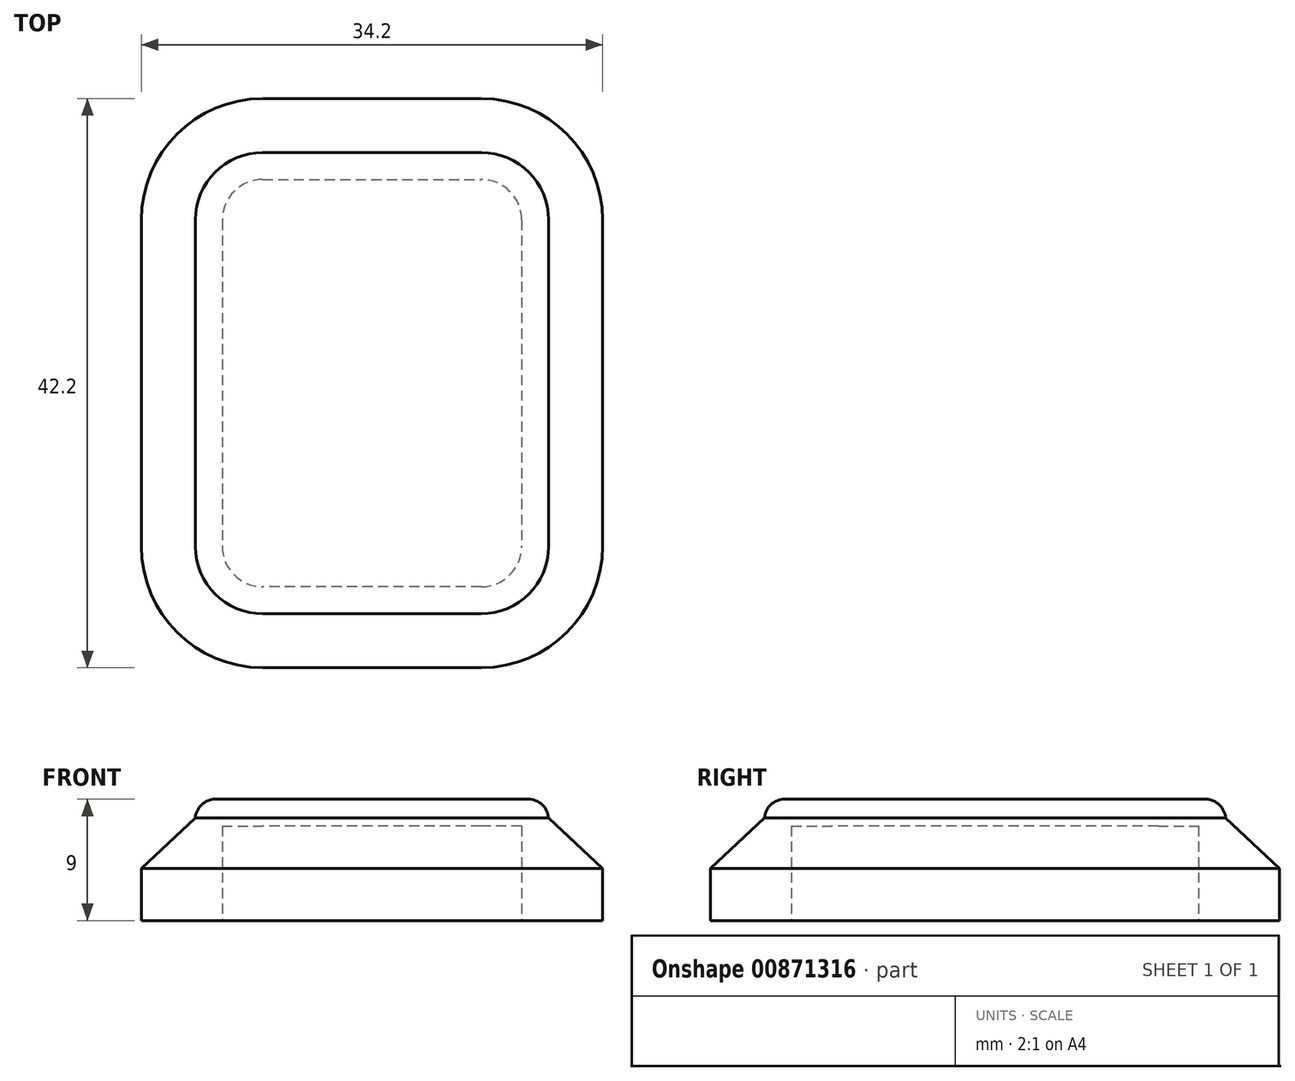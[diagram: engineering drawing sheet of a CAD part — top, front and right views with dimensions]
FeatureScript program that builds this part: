
annotation { "Feature Type Name" : "Feature", "Feature Type Description" : "" }
export const myFeature = defineFeature(function(context is Context, id is Id, definition is map)
    precondition{}
    {
        {
            var Q0;
            Q0=qCreatedBy(makeId("Top.planeOp"),FACE);
            var sketch = newSketch(context, id + "F0", { "sketchPlane" : qUnion([Q0])});
            skLineSegment(sketch, "E0", {"start": v(-8.1, 15.1) * mm, "end": v(8.1, 15.1) * mm});
            skLineSegment(sketch, "E1", {"start": v(11.1, 12.1) * mm, "end": v(11.1, -12.1) * mm});
            skLineSegment(sketch, "E2", {"start": v(8.1, -15.1) * mm, "end": v(-8.1, -15.1) * mm});
            skLineSegment(sketch, "E3", {"start": v(-11.1, 12.1) * mm, "end": v(-11.1, -12.1) * mm});
            skPoint(sketch, "E4.visualSharp", {"position": v(-11.1, 15.1) * mm});
            skArc(sketch, "E4.filletArc", {"start": v(-8.1, 15.1) * mm, "mid": v(-10.22, 14.22) * mm, "end": v(-11.1, 12.1) * mm});
            skPoint(sketch, "E5.visualSharp", {"position": v(11.1, 15.1) * mm});
            skArc(sketch, "E5.filletArc", {"start": v(11.1, 12.1) * mm, "mid": v(10.22, 14.22) * mm, "end": v(8.1, 15.1) * mm});
            skPoint(sketch, "E6.visualSharp", {"position": v(11.1, -15.1) * mm});
            skArc(sketch, "E6.filletArc", {"start": v(8.1, -15.1) * mm, "mid": v(10.22, -14.22) * mm, "end": v(11.1, -12.1) * mm});
            skPoint(sketch, "E7.visualSharp", {"position": v(-11.1, -15.1) * mm});
            skArc(sketch, "E7.filletArc", {"start": v(-11.1, -12.1) * mm, "mid": v(-10.22, -14.22) * mm, "end": v(-8.1, -15.1) * mm});
            skArc(sketch, "E8.0", {"start": v(-8.1, 17.1) * mm, "mid": v(-11.64, 15.64) * mm, "end": v(-13.1, 12.1) * mm});
            skLineSegment(sketch, "E8.1", {"start": v(-13.1, 12.1) * mm, "end": v(-13.1, -12.1) * mm});
            skLineSegment(sketch, "E8.2", {"start": v(-8.1, 17.1) * mm, "end": v(8.1, 17.1) * mm});
            skArc(sketch, "E8.3", {"start": v(-13.1, -12.1) * mm, "mid": v(-11.64, -15.64) * mm, "end": v(-8.1, -17.1) * mm});
            skArc(sketch, "E8.4", {"start": v(13.1, 12.1) * mm, "mid": v(11.64, 15.64) * mm, "end": v(8.1, 17.1) * mm});
            skLineSegment(sketch, "E8.5", {"start": v(13.1, 12.1) * mm, "end": v(13.1, -12.1) * mm});
            skArc(sketch, "E8.6", {"start": v(8.1, -17.1) * mm, "mid": v(11.64, -15.64) * mm, "end": v(13.1, -12.1) * mm});
            skLineSegment(sketch, "E8.7", {"start": v(8.1, -17.1) * mm, "end": v(-8.1, -17.1) * mm});
            skSolve(sketch);
        }
        {
            var Q0;
            Q0 = qSketchRegion(id + "F0", true);
            extrude(context, id + "F1", {"entities" : qUnion([Q0]), "depth" : 7 * mm, "offsetDistance" : 25 * mm});
        }
        {
            var Q0;
            Q0=makeQuery(id+"F1.opExtrude","CAP_FACE",FACE,{"disambiguationData":[OSD([sQuery(id+"F0.wireOp",EDGE,"E0"),sQuery(id+"F0.wireOp",EDGE,"E1"),sQuery(id+"F0.wireOp",EDGE,"E2"),sQuery(id+"F0.wireOp",EDGE,"E3"),sQuery(id+"F0.wireOp",EDGE,"E4.filletArc"),sQuery(id+"F0.wireOp",EDGE,"E5.filletArc"),sQuery(id+"F0.wireOp",EDGE,"E6.filletArc"),sQuery(id+"F0.wireOp",EDGE,"E7.filletArc"),sQuery(id+"F0.wireOp",EDGE,"E8.0"),sQuery(id+"F0.wireOp",EDGE,"E8.1"),sQuery(id+"F0.wireOp",EDGE,"E8.2"),sQuery(id+"F0.wireOp",EDGE,"E8.3"),sQuery(id+"F0.wireOp",EDGE,"E8.4"),sQuery(id+"F0.wireOp",EDGE,"E8.5"),sQuery(id+"F0.wireOp",EDGE,"E8.6"),sQuery(id+"F0.wireOp",EDGE,"E8.7")])],"isStart":false});
            var sketch = newSketch(context, id + "F2", { "sketchPlane" : qUnion([Q0])});
            skArc(sketch, "E9.0", {"start": v(-8.1, 17.1) * mm, "mid": v(-11.64, 15.64) * mm, "end": v(-13.1, 12.1) * mm});
            skLineSegment(sketch, "E9.1", {"start": v(-13.1, 12.1) * mm, "end": v(-13.1, -12.1) * mm});
            skLineSegment(sketch, "E9.2", {"start": v(-8.1, 17.1) * mm, "end": v(8.1, 17.1) * mm});
            skArc(sketch, "E9.3", {"start": v(-13.1, -12.1) * mm, "mid": v(-11.64, -15.64) * mm, "end": v(-8.1, -17.1) * mm});
            skArc(sketch, "E9.4", {"start": v(13.1, 12.1) * mm, "mid": v(11.64, 15.64) * mm, "end": v(8.1, 17.1) * mm});
            skLineSegment(sketch, "E9.5", {"start": v(13.1, 12.1) * mm, "end": v(13.1, -12.1) * mm});
            skArc(sketch, "E9.6", {"start": v(8.1, -17.1) * mm, "mid": v(11.64, -15.64) * mm, "end": v(13.1, -12.1) * mm});
            skLineSegment(sketch, "E9.7", {"start": v(8.1, -17.1) * mm, "end": v(-8.1, -17.1) * mm});
            skSolve(sketch);
        }
        {
            var Q0;
            Q0 = qSketchRegion(id + "F2", true);
            extrude(context, id + "F3", {"entities" : qUnion([Q0]), "operationType" : NewBodyOperationType.ADD, "depth" : 2 * mm, "offsetDistance" : 25 * mm});
        }
        {
            var Q0;
            Q0=makeQuery(id+"F3.opExtrude","CAP_EDGE",EDGE,{"disambiguationData":[OSD([sQuery(id+"F2.wireOp",EDGE,"E9.1")])],"isStart":false});
            fillet(context, id + "F4", {"entities" : qUnion([Q0]), "radius" : 1.5 * mm, "tangentPropagation" : true, "allowEdgeOverflow" : false});
        }
        {
            var Q0;
            Q0=makeQuery(id+"F1.opExtrude","CAP_FACE",FACE,{"disambiguationData":[OSD([sQuery(id+"F0.wireOp",EDGE,"E0"),sQuery(id+"F0.wireOp",EDGE,"E1"),sQuery(id+"F0.wireOp",EDGE,"E2"),sQuery(id+"F0.wireOp",EDGE,"E3"),sQuery(id+"F0.wireOp",EDGE,"E4.filletArc"),sQuery(id+"F0.wireOp",EDGE,"E5.filletArc"),sQuery(id+"F0.wireOp",EDGE,"E6.filletArc"),sQuery(id+"F0.wireOp",EDGE,"E7.filletArc"),sQuery(id+"F0.wireOp",EDGE,"E8.0"),sQuery(id+"F0.wireOp",EDGE,"E8.1"),sQuery(id+"F0.wireOp",EDGE,"E8.2"),sQuery(id+"F0.wireOp",EDGE,"E8.3"),sQuery(id+"F0.wireOp",EDGE,"E8.4"),sQuery(id+"F0.wireOp",EDGE,"E8.5"),sQuery(id+"F0.wireOp",EDGE,"E8.6"),sQuery(id+"F0.wireOp",EDGE,"E8.7")])],"isStart":true});
            var sketch = newSketch(context, id + "F5", { "sketchPlane" : qUnion([Q0])});
            skArc(sketch, "E10.0", {"start": v(-8.1, -21.1) * mm, "mid": v(-14.46, -18.46) * mm, "end": v(-17.1, -12.1) * mm});
            skLineSegment(sketch, "E10.1", {"start": v(-8.1, -21.1) * mm, "end": v(8.1, -21.1) * mm});
            skLineSegment(sketch, "E10.2", {"start": v(-17.1, -12.1) * mm, "end": v(-17.1, 12.1) * mm});
            skArc(sketch, "E10.3", {"start": v(17.1, -12.1) * mm, "mid": v(14.46, -18.46) * mm, "end": v(8.1, -21.1) * mm});
            skArc(sketch, "E10.4", {"start": v(-17.1, 12.1) * mm, "mid": v(-14.46, 18.46) * mm, "end": v(-8.1, 21.1) * mm});
            skLineSegment(sketch, "E10.5", {"start": v(8.1, 21.1) * mm, "end": v(-8.1, 21.1) * mm});
            skArc(sketch, "E10.6", {"start": v(8.1, 21.1) * mm, "mid": v(14.46, 18.46) * mm, "end": v(17.1, 12.1) * mm});
            skLineSegment(sketch, "E10.7", {"start": v(17.1, -12.1) * mm, "end": v(17.1, 12.1) * mm});
            skArc(sketch, "E11.0", {"start": v(-8.1, -15.1) * mm, "mid": v(-10.22, -14.22) * mm, "end": v(-11.1, -12.1) * mm});
            skLineSegment(sketch, "E11.1", {"start": v(-11.1, -12.1) * mm, "end": v(-11.1, 12.1) * mm});
            skLineSegment(sketch, "E11.2", {"start": v(-8.1, -15.1) * mm, "end": v(8.1, -15.1) * mm});
            skArc(sketch, "E11.3", {"start": v(-11.1, 12.1) * mm, "mid": v(-10.22, 14.22) * mm, "end": v(-8.1, 15.1) * mm});
            skArc(sketch, "E11.4", {"start": v(11.1, -12.1) * mm, "mid": v(10.22, -14.22) * mm, "end": v(8.1, -15.1) * mm});
            skLineSegment(sketch, "E11.5", {"start": v(11.1, -12.1) * mm, "end": v(11.1, 12.1) * mm});
            skArc(sketch, "E11.6", {"start": v(8.1, 15.1) * mm, "mid": v(10.22, 14.22) * mm, "end": v(11.1, 12.1) * mm});
            skLineSegment(sketch, "E11.7", {"start": v(8.1, 15.1) * mm, "end": v(-8.1, 15.1) * mm});
            skSolve(sketch);
        }
        {
            var Q0;
            Q0 = qSketchRegion(id + "F5", true);
            extrude(context, id + "F6", {"entities" : qUnion([Q0]), "operationType" : NewBodyOperationType.ADD, "oppositeDirection" : true, "depth" : 2 * mm, "offsetDistance" : 25 * mm});
        }
        {
            var Q0;
            Q0=makeQuery(id+"F3.boolean.opBoolean","MERGE",FACE,{"derivedFrom":[makeQuery(id+"F1.opExtrude","SWEPT_FACE",FACE,{"disambiguationData":[OSD([sQuery(id+"F0.wireOp",EDGE,"E8.2")])]}),makeQuery(id+"F3.opExtrude","SWEPT_FACE",FACE,{"disambiguationData":[OSD([sQuery(id+"F2.wireOp",EDGE,"E9.2")])]})]});
            var Q1;
            Q1=makeQuery(id+"F6.boolean.opBoolean","INTERSECT",EDGE,{"derivedFrom":[makeQuery(id+"F3.boolean.opBoolean","MERGE",FACE,{"derivedFrom":[makeQuery(id+"F1.opExtrude","SWEPT_FACE",FACE,{"disambiguationData":[OSD([sQuery(id+"F0.wireOp",EDGE,"E8.2")])]}),makeQuery(id+"F3.opExtrude","SWEPT_FACE",FACE,{"disambiguationData":[OSD([sQuery(id+"F2.wireOp",EDGE,"E9.2")])]})]}),makeQuery(id+"F6.opExtrude","CAP_FACE",FACE,{"disambiguationData":[OSD([sQuery(id+"F5.wireOp",EDGE,"E10.0"),sQuery(id+"F5.wireOp",EDGE,"E10.1"),sQuery(id+"F5.wireOp",EDGE,"E10.2"),sQuery(id+"F5.wireOp",EDGE,"E10.3"),sQuery(id+"F5.wireOp",EDGE,"E10.4"),sQuery(id+"F5.wireOp",EDGE,"E10.5"),sQuery(id+"F5.wireOp",EDGE,"E10.6"),sQuery(id+"F5.wireOp",EDGE,"E10.7"),sQuery(id+"F5.wireOp",EDGE,"E11.0"),sQuery(id+"F5.wireOp",EDGE,"E11.1"),sQuery(id+"F5.wireOp",EDGE,"E11.2"),sQuery(id+"F5.wireOp",EDGE,"E11.3"),sQuery(id+"F5.wireOp",EDGE,"E11.4"),sQuery(id+"F5.wireOp",EDGE,"E11.5"),sQuery(id+"F5.wireOp",EDGE,"E11.6"),sQuery(id+"F5.wireOp",EDGE,"E11.7")])],"isStart":false})]});
            chamfer(context, id + "F7", {"entities" : qUnion([Q0, Q1]), "width" : 6 * mm, "tangentPropagation" : true});
        }
    });
